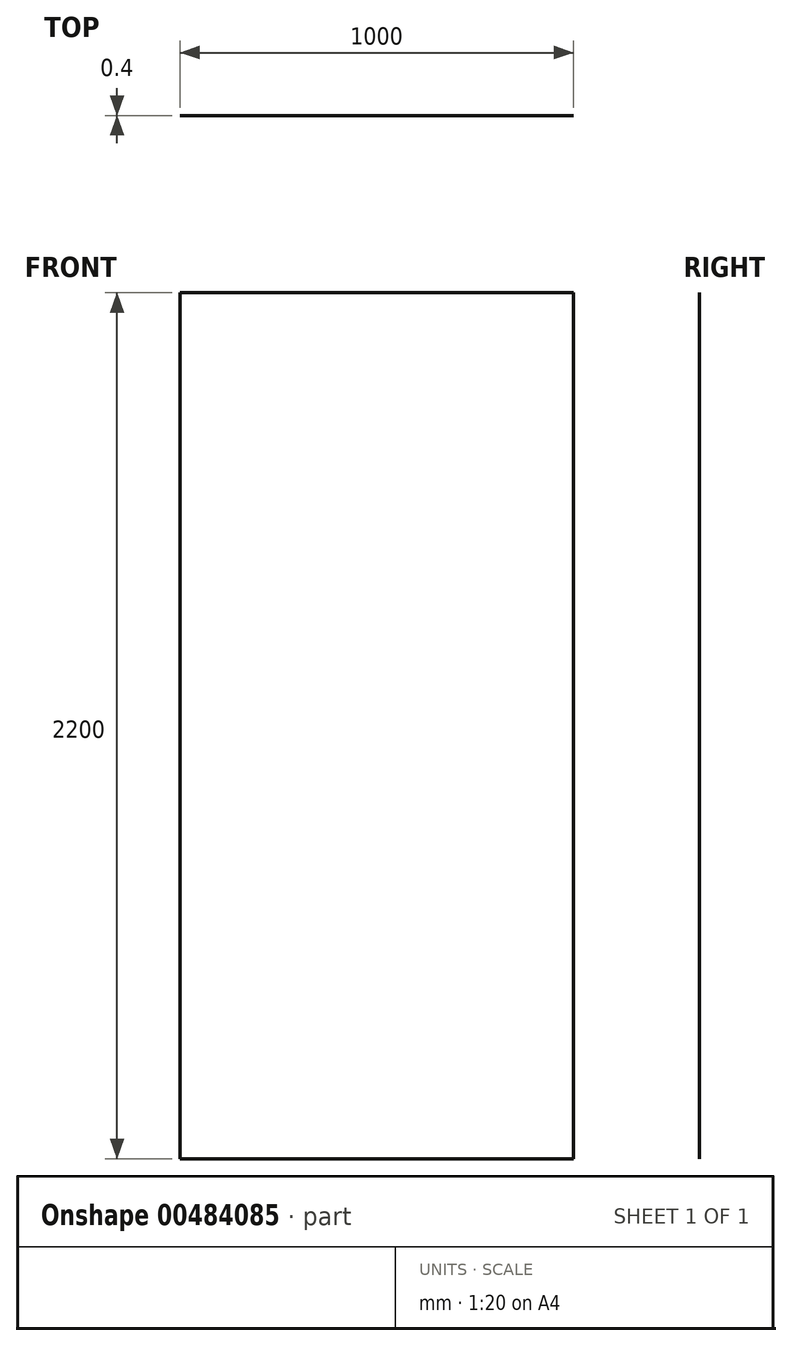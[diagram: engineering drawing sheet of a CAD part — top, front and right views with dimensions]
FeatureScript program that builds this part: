
annotation { "Feature Type Name" : "Feature", "Feature Type Description" : "" }
export const myFeature = defineFeature(function(context is Context, id is Id, definition is map)
    precondition{}
    {
        {
            var Q0;
            Q0=qCreatedBy(makeId("Top.planeOp"),FACE);
            var sketch = newSketch(context, id + "F0", { "sketchPlane" : qUnion([Q0])});
            skLineSegment(sketch, "E0.bottom", {"start": v(-8309.78, -127.36) * mm, "end": v(-7309.78, -127.36) * mm});
            skLineSegment(sketch, "E0.top", {"start": v(-8309.78, -127.76) * mm, "end": v(-7309.78, -127.76) * mm});
            skLineSegment(sketch, "E0.left", {"start": v(-8309.78, -127.36) * mm, "end": v(-8309.78, -127.76) * mm});
            skLineSegment(sketch, "E0.right", {"start": v(-7309.78, -127.36) * mm, "end": v(-7309.78, -127.76) * mm});
            skSolve(sketch);
        }
        {
            var Q0;
            Q0 = qSketchRegion(id + "F0", true);
            extrude(context, id + "F1", {"entities" : qUnion([Q0]), "depth" : 2200 * mm});
        }
    });
